FCSTD DOCUMENT  (FreeCAD 0.21R33771 (Git))
Label: basic-sketcher
License: All rights reserved
LicenseURL: http://en.wikipedia.org/wiki/All_rights_reserved
objects: Sketcher::SketchObject×1
note: 1 computed .brp shape members not serialized (recipe doc carries the construction recipe); baked Part::Feature solids carry a one-line shape summary decoded from their .brp

FEATURE [Sketcher::SketchObject] Sketch
  FullyConstrained = false
  sketch-geometry (16):
    g0: LineSegment StartX=0.0409265 StartY=0.0442954 StartZ=0 EndX=20.7018 EndY=21.8346 EndZ=0
    g1: LineSegment StartX=-0.0156633 StartY=0.00981101 StartZ=0 EndX=25.6367 EndY=-15.5993 EndZ=0
    g2: LineSegment StartX=2.69271e-10 StartY=0.0412523 StartZ=0 EndX=0 EndY=-29.9868 EndZ=0
    g3: LineSegment StartX=-0.00362834 StartY=-0.00428834 StartZ=0 EndX=-20.6661 EndY=-21.7931 EndZ=0
    g4: Circle CenterX=0.0111656 CenterY=-0.0654645 CenterZ=0 NormalX=0 NormalY=0 NormalZ=1 AngleXU=0 Radius=7.99948
    g5: ArcOfCircle CenterX=20.7018 CenterY=21.8346 CenterZ=0 NormalX=0 NormalY=0 NormalZ=1 AngleXU=0 Radius=6.64183 StartAngle=5.85497 EndAngle=8.90203
    g6: ArcOfCircle CenterX=0 CenterY=-29.9868 CenterZ=0 NormalX=0 NormalY=0 NormalZ=1 AngleXU=0 Radius=6.64183 StartAngle=3.15599 EndAngle=6.27755
    g7: ArcOfCircle CenterX=25.6367 CenterY=-15.5993 CenterZ=0 NormalX=0 NormalY=0 NormalZ=1 AngleXU=0 Radius=6.64183 StartAngle=4.27238 EndAngle=7.43772
    g8: ArcOfCircle CenterX=-20.6661 CenterY=-21.7931 CenterZ=0 NormalX=0 NormalY=0 NormalZ=1 AngleXU=0 Radius=6.64183 StartAngle=2.59503 EndAngle=5.9525
    g9: LineSegment StartX=0.0111656 StartY=-0.0654645 StartZ=0 EndX=-21.9739 EndY=20.388 EndZ=0
    g10: ArcOfCircle CenterX=-21.9739 CenterY=20.388 CenterZ=0 NormalX=0 NormalY=0 NormalZ=1 AngleXU=0 Radius=6.64183 StartAngle=0.392256 EndAngle=4.1717
    g11: ArcOfCircle CenterX=0 CenterY=29.4785 CenterZ=0 NormalX=0 NormalY=0 NormalZ=1 AngleXU=0 Radius=17.1382 StartAngle=3.53385 EndAngle=5.98315
    g12: ArcOfCircle CenterX=39.65 CenterY=4.78785 CenterZ=0 NormalX=0 NormalY=0 NormalZ=1 AngleXU=0 Radius=17.1382 StartAngle=2.4369 EndAngle=3.99803
    g13: ArcOfCircle CenterX=19.819 CenterY=-32.0477 CenterZ=0 NormalX=0 NormalY=0 NormalZ=1 AngleXU=0 Radius=17.1382 StartAngle=1.57851 EndAngle=2.94719
    g14: ArcOfCircle CenterX=-14.3918 CenterY=-32.8948 CenterZ=0 NormalX=0 NormalY=0 NormalZ=1 AngleXU=0 Radius=17.1382 StartAngle=0.216346 EndAngle=1.48325
    g15: ArcOfCircle CenterX=-34.2141 CenterY=0 CenterZ=0 NormalX=0 NormalY=0 NormalZ=1 AngleXU=0 Radius=17.1382 StartAngle=5.18225 EndAngle=7.3133
  constraints (23):
    c: PointOnObject(g2,g-2)
    c: Coincident(g5,g0)
    c: Coincident(g6,g2)
    c: Coincident(g7,g1)
    c: Coincident(g8,g3)
    c: Coincident(g9,g4)
    c: Coincident(g10,g9)
    c: PointOnObject(g11,g-2)
    c: PointOnObject(g15,g-1)
    c: Equal(g0,g1)
    c: Equal(g1,g2)
    c: Equal(g2,g3)
    c: Equal(g3,g9)
    c: Equal(g5,g6)
    c: Equal(g6,g7)
    c: Equal(g7,g8)
    c: Equal(g8,g10)
    c: Equal(g11,g12)
    c: Equal(g12,g13)
    c: Equal(g13,g14)
    c: Equal(g14,g15)
    c: Tangent(g10,g11) = 1.5708
    c: Tangent(g10,g15) = 1.5708
